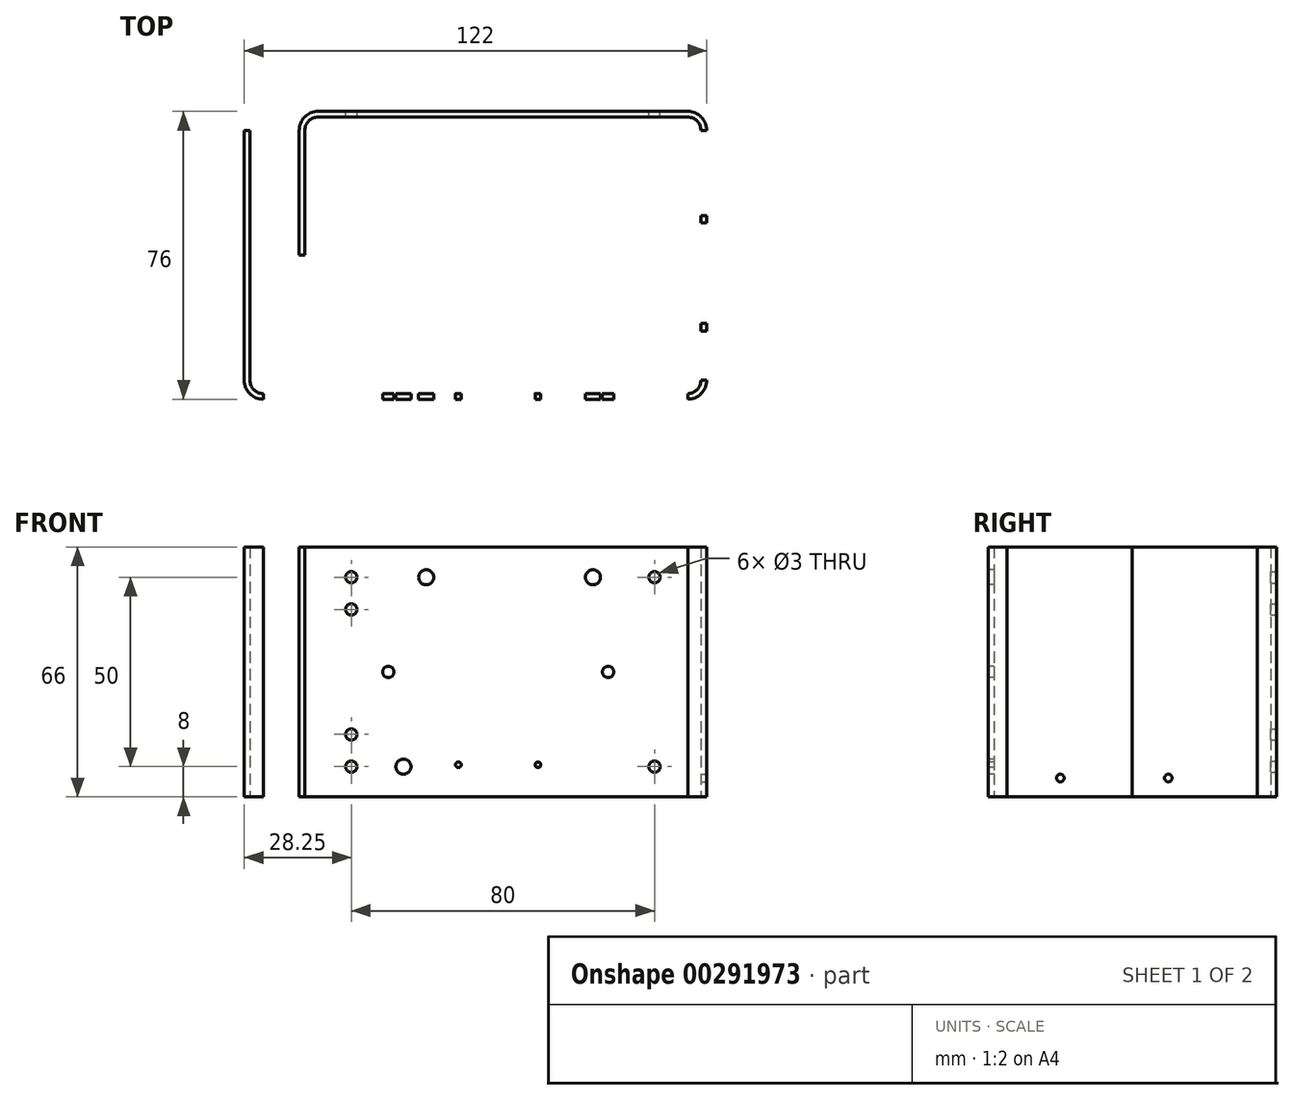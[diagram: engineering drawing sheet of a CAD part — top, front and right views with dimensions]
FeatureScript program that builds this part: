
annotation { "Feature Type Name" : "Feature", "Feature Type Description" : "" }
export const myFeature = defineFeature(function(context is Context, id is Id, definition is map)
    precondition{}
    {
        {
            var Q0;
            Q0=qCreatedBy(makeId("Top.planeOp"),FACE);
            var sketch = newSketch(context, id + "F0", { "sketchPlane" : qUnion([Q0])});
            skLineSegment(sketch, "E0", {"start": v(-66.75, 33) * mm, "end": v(-66.75, -33) * mm});
            skLineSegment(sketch, "E1", {"start": v(-63.25, -36.5) * mm, "end": v(48.75, -36.5) * mm});
            skLineSegment(sketch, "E2", {"start": v(52.25, -33) * mm, "end": v(52.25, 33) * mm});
            skLineSegment(sketch, "E3", {"start": v(48.75, 36.5) * mm, "end": v(-48.75, 36.5) * mm});
            skLineSegment(sketch, "E4", {"start": v(-52.25, 33) * mm, "end": v(-52.25, 0) * mm});
            skLineSegment(sketch, "E5.0", {"start": v(-53.75, 33) * mm, "end": v(-53.75, 0) * mm});
            skLineSegment(sketch, "E5.1", {"start": v(-68.25, 33) * mm, "end": v(-68.25, -33) * mm});
            skLineSegment(sketch, "E5.2", {"start": v(-63.25, -38) * mm, "end": v(48.75, -38) * mm});
            skLineSegment(sketch, "E5.3", {"start": v(53.75, -33) * mm, "end": v(53.75, 33) * mm});
            skLineSegment(sketch, "E5.4", {"start": v(48.75, 38) * mm, "end": v(-48.75, 38) * mm});
            skLineSegment(sketch, "E6", {"start": v(-52.25, 0) * mm, "end": v(-53.75, 0) * mm});
            skLineSegment(sketch, "E7", {"start": v(-66.75, 33) * mm, "end": v(-68.25, 33) * mm});
            skPoint(sketch, "E8.visualSharp", {"position": v(-66.75, -36.5) * mm});
            skArc(sketch, "E8.filletArc", {"start": v(-66.75, -33) * mm, "mid": v(-65.72, -35.47) * mm, "end": v(-63.25, -36.5) * mm});
            skPoint(sketch, "E9.visualSharp", {"position": v(52.25, -36.5) * mm});
            skArc(sketch, "E9.filletArc", {"start": v(48.75, -36.5) * mm, "mid": v(51.22, -35.47) * mm, "end": v(52.25, -33) * mm});
            skPoint(sketch, "E10.visualSharp", {"position": v(52.25, 36.5) * mm});
            skArc(sketch, "E10.filletArc", {"start": v(52.25, 33) * mm, "mid": v(51.22, 35.47) * mm, "end": v(48.75, 36.5) * mm});
            skPoint(sketch, "E11.visualSharp", {"position": v(-52.25, 36.5) * mm});
            skArc(sketch, "E11.filletArc", {"start": v(-48.75, 36.5) * mm, "mid": v(-51.22, 35.47) * mm, "end": v(-52.25, 33) * mm});
            skPoint(sketch, "E12.visualSharp", {"position": v(-68.25, -38) * mm});
            skArc(sketch, "E12.filletArc", {"start": v(-68.25, -33) * mm, "mid": v(-66.79, -36.54) * mm, "end": v(-63.25, -38) * mm});
            skPoint(sketch, "E13.visualSharp", {"position": v(53.75, -38) * mm});
            skArc(sketch, "E13.filletArc", {"start": v(48.75, -38) * mm, "mid": v(52.29, -36.54) * mm, "end": v(53.75, -33) * mm});
            skPoint(sketch, "E14.visualSharp", {"position": v(53.75, 38) * mm});
            skArc(sketch, "E14.filletArc", {"start": v(53.75, 33) * mm, "mid": v(52.29, 36.54) * mm, "end": v(48.75, 38) * mm});
            skPoint(sketch, "E15.visualSharp", {"position": v(-53.75, 38) * mm});
            skArc(sketch, "E15.filletArc", {"start": v(-48.75, 38) * mm, "mid": v(-52.29, 36.54) * mm, "end": v(-53.75, 33) * mm});
            skLineSegment(sketch, "E16", {"start": v(52.25, 0) * mm, "end": v(-12.48, 0) * mm, "construction": true});
            skLineSegment(sketch, "E17", {"start": v(0, 36.5) * mm, "end": v(0, -15.26) * mm, "construction": true});
            skSolve(sketch);
        }
        {
            var Q0;
            Q0=qSketchRegion(id+"F0",true);
            extrude(context, id + "F1", {"entities" : qUnion([Q0]), "depth" : 66 * mm});
        }
        {
            var Q0;
            Q0=makeQuery(id+"F1.opExtrude","SWEPT_FACE",FACE,{"disambiguationData":[OSD([sQuery(id+"F0.wireOp",EDGE,"E5.2")])]});
            var sketch = newSketch(context, id + "F2", { "sketchPlane" : qUnion([Q0])});
            skLineSegment(sketch, "E18.bottom", {"start": v(-23.25, 52) * mm, "end": v(20.75, 52) * mm});
            skLineSegment(sketch, "E18.top", {"start": v(-23.25, 14) * mm, "end": v(20.75, 14) * mm});
            skLineSegment(sketch, "E18.left", {"start": v(-26.25, 49) * mm, "end": v(-26.25, 17) * mm});
            skLineSegment(sketch, "E18.right", {"start": v(23.75, 49) * mm, "end": v(23.75, 17) * mm});
            skLineSegment(sketch, "E19", {"start": v(-63.25, 33) * mm, "end": v(43.75, 33) * mm, "construction": true});
            skLineSegment(sketch, "E20", {"start": v(23.75, 33) * mm, "end": v(-26.25, 33) * mm, "construction": true});
            skLineSegment(sketch, "E21", {"start": v(-1.25, 52) * mm, "end": v(-1.25, 14) * mm, "construction": true});
            skLineSegment(sketch, "E22", {"start": v(-7.25, 66) * mm, "end": v(-7.25, 0) * mm, "construction": true});
            skPoint(sketch, "E23.visualSharp", {"position": v(-26.25, 52) * mm});
            skArc(sketch, "E23.filletArc", {"start": v(-23.25, 52) * mm, "mid": v(-25.37, 51.12) * mm, "end": v(-26.25, 49) * mm});
            skPoint(sketch, "E24.visualSharp", {"position": v(23.75, 52) * mm});
            skArc(sketch, "E24.filletArc", {"start": v(23.75, 49) * mm, "mid": v(22.87, 51.12) * mm, "end": v(20.75, 52) * mm});
            skPoint(sketch, "E25.visualSharp", {"position": v(23.75, 14) * mm});
            skArc(sketch, "E25.filletArc", {"start": v(20.75, 14) * mm, "mid": v(22.87, 14.88) * mm, "end": v(23.75, 17) * mm});
            skPoint(sketch, "E26.visualSharp", {"position": v(-26.25, 14) * mm});
            skArc(sketch, "E26.filletArc", {"start": v(-26.25, 17) * mm, "mid": v(-25.37, 14.88) * mm, "end": v(-23.25, 14) * mm});
            skCircle(sketch, "E27", {"center": v(-30.25, 33) * mm, "radius": 1.5 * mm});
            skCircle(sketch, "E28.MirrorC", {"center": v(27.75, 33) * mm, "radius": 1.5 * mm});
            skCircle(sketch, "E29", {"center": v(-26.25, 58) * mm, "radius": 2 * mm});
            skCircle(sketch, "E30.MirrorC", {"center": v(23.75, 58) * mm, "radius": 2 * mm});
            skCircle(sketch, "E31.MirrorC", {"center": v(-26.25, 8) * mm, "radius": 2 * mm});
            skCircle(sketch, "E32.MirrorC", {"center": v(23.75, 8) * mm, "radius": 2 * mm});
            skLineSegment(sketch, "E33.bottom", {"start": v(-7.25, 7) * mm, "end": v(4.75, 7) * mm});
            skPoint(sketch, "E34.visualSharp", {"position": v(6.25, 10) * mm});
            skLineSegment(sketch, "E33.top", {"start": v(-7.25, 10) * mm, "end": v(4.75, 10) * mm});
            skArc(sketch, "E35.filletArc", {"start": v(-7.25, 10) * mm, "mid": v(-8.31, 9.56) * mm, "end": v(-8.75, 8.5) * mm});
            skLineSegment(sketch, "E33.left", {"start": v(-8.75, 8.5) * mm, "end": v(-8.75, 8.5) * mm});
            skLineSegment(sketch, "E33.right", {"start": v(6.25, 8.5) * mm, "end": v(6.25, 8.5) * mm});
            skArc(sketch, "E36.filletArc", {"start": v(-8.75, 8.5) * mm, "mid": v(-8.31, 7.44) * mm, "end": v(-7.25, 7) * mm});
            skArc(sketch, "E37.filletArc", {"start": v(4.75, 7) * mm, "mid": v(5.81, 7.44) * mm, "end": v(6.25, 8.5) * mm});
            skArc(sketch, "E34.filletArc", {"start": v(6.25, 8.5) * mm, "mid": v(5.81, 9.56) * mm, "end": v(4.75, 10) * mm});
            skCircle(sketch, "E38", {"center": v(-11.75, 8.5) * mm, "radius": 0.75 * mm});
            skPoint(sketch, "E39", {"position": v(-1.25, 10) * mm});
            skLineSegment(sketch, "E40", {"start": v(-11.75, 8.5) * mm, "end": v(6.89, 8.5) * mm, "construction": true});
            skPoint(sketch, "E35.visualSharp", {"position": v(-8.75, 10) * mm});
            skPoint(sketch, "E36.visualSharp", {"position": v(-8.75, 7) * mm});
            skPoint(sketch, "E37.visualSharp", {"position": v(6.25, 7) * mm});
            skLineSegment(sketch, "E41", {"start": v(-1.25, 10) * mm, "end": v(-1.25, 7) * mm, "construction": true});
            skCircle(sketch, "E42.MirrorC", {"center": v(9.25, 8.5) * mm, "radius": 0.75 * mm});
            skLineSegment(sketch, "E43", {"start": v(-26.25, 8) * mm, "end": v(-26.25, 58) * mm, "construction": true});
            skLineSegment(sketch, "E44", {"start": v(23.75, 58) * mm, "end": v(23.75, 8) * mm, "construction": true});
            skLineSegment(sketch, "E45", {"start": v(-26.25, 8) * mm, "end": v(23.75, 8) * mm, "construction": true});
            skLineSegment(sketch, "E46", {"start": v(23.75, 58) * mm, "end": v(-26.25, 58) * mm, "construction": true});
            skCircle(sketch, "E47", {"center": v(-20.25, 8) * mm, "radius": 2 * mm});
            skCircle(sketch, "E48.MirrorC", {"center": v(-20.25, 58) * mm, "radius": 2 * mm});
            skCircle(sketch, "E49.MirrorC", {"center": v(17.75, 58) * mm, "radius": 2 * mm});
            skCircle(sketch, "E50", {"center": v(14.75, 8) * mm, "radius": 2 * mm});
            skPoint(sketch, "E51", {"position": v(-63.25, 33) * mm});
            skSolve(sketch);
        }
        {
            var Q0;
            Q0=makeQuery(id+"F2.imprint","IMPRINT",FACE,{"disambiguationData":[TD([[makeQuery(id+"F2.imprint","IMPRINT",EDGE,{"derivedFrom":sQuery(id+"F2.wireOp",EDGE,"E18.bottom")}),-1.0]])]});
            var Q1;
            Q1=makeQuery(id+"F2.imprint","IMPRINT",FACE,{"disambiguationData":[TD([[makeQuery(id+"F2.imprint","IMPRINT",EDGE,{"derivedFrom":sQuery(id+"F2.wireOp",EDGE,"5223969e-9384-4705-a09f-08a9d0864926")}),1.0]])]});
            var Q2;
            Q2=makeQuery(id+"F2.imprint","IMPRINT",FACE,{"disambiguationData":[TD([[makeQuery(id+"F2.imprint","IMPRINT",EDGE,{"derivedFrom":sQuery(id+"F2.wireOp",EDGE,"b6238159-0034-45e9-8c88-9dabcd8353630.MirrorC")}),-1.0]])]});
            var Q3;
            Q3=makeQuery(id+"F2.imprint","IMPRINT",FACE,{"disambiguationData":[TD([[makeQuery(id+"F2.imprint","IMPRINT",EDGE,{"derivedFrom":sQuery(id+"F2.wireOp",EDGE,"E29")}),1.0]])]});
            var Q4;
            Q4=makeQuery(id+"F2.imprint","IMPRINT",FACE,{"disambiguationData":[TD([[makeQuery(id+"F2.imprint","IMPRINT",EDGE,{"derivedFrom":sQuery(id+"F2.wireOp",EDGE,"E30.MirrorC")}),-1.0]])]});
            var Q5;
            Q5=makeQuery(id+"F2.imprint","IMPRINT",FACE,{"disambiguationData":[TD([[makeQuery(id+"F2.imprint","IMPRINT",EDGE,{"derivedFrom":sQuery(id+"F2.wireOp",EDGE,"E32.MirrorC")}),1.0]])]});
            var Q6;
            Q6=makeQuery(id+"F2.imprint","IMPRINT",FACE,{"disambiguationData":[TD([[makeQuery(id+"F2.imprint","IMPRINT",EDGE,{"derivedFrom":sQuery(id+"F2.wireOp",EDGE,"E31.MirrorC")}),-1.0]])]});
            var Q7;
            Q7=makeQuery(id+"F2.imprint","IMPRINT",FACE,{"disambiguationData":[TD([[makeQuery(id+"F2.imprint","IMPRINT",EDGE,{"derivedFrom":sQuery(id+"F2.wireOp",EDGE,"E33.bottom")}),1.0]])]});
            var Q8;
            Q8=makeQuery(id+"F2.imprint","IMPRINT",FACE,{"disambiguationData":[TD([[makeQuery(id+"F2.imprint","IMPRINT",EDGE,{"derivedFrom":sQuery(id+"F2.wireOp",EDGE,"E47")}),1.0]])]});
            var Q9;
            Q9=makeQuery(id+"F2.imprint","IMPRINT",FACE,{"disambiguationData":[TD([[makeQuery(id+"F2.imprint","IMPRINT",EDGE,{"derivedFrom":sQuery(id+"F2.wireOp",EDGE,"E48.MirrorC")}),-1.0]])]});
            var Q10;
            Q10=makeQuery(id+"F2.imprint","IMPRINT",FACE,{"disambiguationData":[TD([[makeQuery(id+"F2.imprint","IMPRINT",EDGE,{"derivedFrom":sQuery(id+"F2.wireOp",EDGE,"E49.MirrorC")}),1.0]])]});
            var Q11;
            Q11=makeQuery(id+"F2.imprint","IMPRINT",FACE,{"disambiguationData":[TD([[makeQuery(id+"F2.imprint","IMPRINT",EDGE,{"derivedFrom":sQuery(id+"F2.wireOp",EDGE,"E50")}),1.0]])]});
            extrude(context, id + "F3", {"entities" : qUnion([Q0, Q1, Q2, Q3, Q4, Q5, Q6, Q7, Q8, Q9, Q10, Q11]), "operationType" : NewBodyOperationType.REMOVE, "oppositeDirection" : true, "depth" : 25 * mm});
        }
        {
            var Q0;
            Q0=makeQuery(id+"F1.opExtrude","SWEPT_FACE",FACE,{"disambiguationData":[OSD([sQuery(id+"F0.wireOp",EDGE,"E5.4")])]});
            var sketch = newSketch(context, id + "F4", { "sketchPlane" : qUnion([Q0])});
            skCircle(sketch, "E52", {"center": v(-40, 58) * mm, "radius": 1.5 * mm});
            skLineSegment(sketch, "E53", {"start": v(-40, 58) * mm, "end": v(-40, 8) * mm, "construction": true});
            skLineSegment(sketch, "E54", {"start": v(-40, 8) * mm, "end": v(40, 8) * mm, "construction": true});
            skLineSegment(sketch, "E55", {"start": v(40, 8) * mm, "end": v(40, 58) * mm, "construction": true});
            skLineSegment(sketch, "E56", {"start": v(40, 58) * mm, "end": v(-40, 58) * mm, "construction": true});
            skCircle(sketch, "E57", {"center": v(-40, 8) * mm, "radius": 1.5 * mm});
            skCircle(sketch, "E58", {"center": v(40, 8) * mm, "radius": 1.5 * mm});
            skCircle(sketch, "E59", {"center": v(40, 58) * mm, "radius": 1.5 * mm});
            skLineSegment(sketch, "E60", {"start": v(0, 0) * mm, "end": v(0, 116) * mm, "construction": true});
            skPoint(sketch, "E60.endSnap0", {"position": v(0, 0) * mm});
            skPoint(sketch, "E61", {"position": v(0, 58) * mm});
            skCircle(sketch, "E62", {"center": v(40, 49.5) * mm, "radius": 1.5 * mm});
            skCircle(sketch, "E63", {"center": v(40, 16.5) * mm, "radius": 1.5 * mm});
            skLineSegment(sketch, "E64", {"start": v(33.75, 66) * mm, "end": v(33.75, 0) * mm, "construction": true});
            skLineSegment(sketch, "E65", {"start": v(33.75, 33) * mm, "end": v(24.95, 33) * mm, "construction": true});
            skLineSegment(sketch, "E66", {"start": v(29.35, 33) * mm, "end": v(29.35, 66) * mm, "construction": true});
            skLineSegment(sketch, "E67", {"start": v(29.35, 33) * mm, "end": v(29.35, 0) * mm, "construction": true});
            skLineSegment(sketch, "E68", {"start": v(29.35, 16.5) * mm, "end": v(44.25, 16.5) * mm, "construction": true});
            skLineSegment(sketch, "E69", {"start": v(29.35, 49.5) * mm, "end": v(45.75, 49.5) * mm, "construction": true});
            skSolve(sketch);
        }
        {
            var Q0;
            Q0=makeQuery(id+"F4.imprint","IMPRINT",FACE,{"disambiguationData":[TD([[makeQuery(id+"F4.imprint","IMPRINT",EDGE,{"derivedFrom":sQuery(id+"F4.wireOp",EDGE,"E52")}),1.0]])]});
            var Q1;
            Q1=makeQuery(id+"F4.imprint","IMPRINT",FACE,{"disambiguationData":[TD([[makeQuery(id+"F4.imprint","IMPRINT",EDGE,{"derivedFrom":sQuery(id+"F4.wireOp",EDGE,"E57")}),1.0]])]});
            var Q2;
            Q2=makeQuery(id+"F4.imprint","IMPRINT",FACE,{"disambiguationData":[TD([[makeQuery(id+"F4.imprint","IMPRINT",EDGE,{"derivedFrom":sQuery(id+"F4.wireOp",EDGE,"E58")}),1.0]])]});
            var Q3;
            Q3=makeQuery(id+"F4.imprint","IMPRINT",FACE,{"disambiguationData":[TD([[makeQuery(id+"F4.imprint","IMPRINT",EDGE,{"derivedFrom":sQuery(id+"F4.wireOp",EDGE,"E59")}),1.0]])]});
            var Q4;
            Q4=makeQuery(id+"F4.imprint","IMPRINT",FACE,{"disambiguationData":[TD([[makeQuery(id+"F4.imprint","IMPRINT",EDGE,{"derivedFrom":sQuery(id+"F4.wireOp",EDGE,"E63")}),1.0]])]});
            var Q5;
            Q5=makeQuery(id+"F4.imprint","IMPRINT",FACE,{"disambiguationData":[TD([[makeQuery(id+"F4.imprint","IMPRINT",EDGE,{"derivedFrom":sQuery(id+"F4.wireOp",EDGE,"E62")}),1.0]])]});
            extrude(context, id + "F5", {"entities" : qUnion([Q0, Q1, Q2, Q3, Q4, Q5]), "operationType" : NewBodyOperationType.REMOVE, "oppositeDirection" : true, "depth" : 25 * mm});
        }
        {
            var Q0;
            Q0=makeQuery(id+"F1.opExtrude","SWEPT_FACE",FACE,{"disambiguationData":[OSD([sQuery(id+"F0.wireOp",EDGE,"E5.3")])]});
            var sketch = newSketch(context, id + "F6", { "sketchPlane" : qUnion([Q0])});
            skLineSegment(sketch, "E70.bottom", {"start": v(-21, 58) * mm, "end": v(-17, 58) * mm});
            skLineSegment(sketch, "E70.top", {"start": v(-21, 8) * mm, "end": v(-17, 8) * mm});
            skLineSegment(sketch, "E70.left", {"start": v(-24, 55) * mm, "end": v(-24, 11) * mm});
            skLineSegment(sketch, "E70.right", {"start": v(-14, 55) * mm, "end": v(-14, 11) * mm});
            skLineSegment(sketch, "E71.bottom", {"start": v(-5, 58) * mm, "end": v(24, 58) * mm});
            skLineSegment(sketch, "E71.top", {"start": v(-5, 8) * mm, "end": v(24, 8) * mm});
            skLineSegment(sketch, "E71.left", {"start": v(-8, 55) * mm, "end": v(-8, 11) * mm});
            skLineSegment(sketch, "E71.right", {"start": v(27, 55) * mm, "end": v(27, 11) * mm});
            skLineSegment(sketch, "E72", {"start": v(-14, 58) * mm, "end": v(-8, 58) * mm, "construction": true});
            skLineSegment(sketch, "E73", {"start": v(-14, 8) * mm, "end": v(-8, 8) * mm, "construction": true});
            skPoint(sketch, "E74.visualSharp", {"position": v(-24, 58) * mm});
            skArc(sketch, "E74.filletArc", {"start": v(-21, 58) * mm, "mid": v(-23.12, 57.12) * mm, "end": v(-24, 55) * mm});
            skPoint(sketch, "E75.visualSharp", {"position": v(-14, 58) * mm});
            skArc(sketch, "E75.filletArc", {"start": v(-14, 55) * mm, "mid": v(-14.88, 57.12) * mm, "end": v(-17, 58) * mm});
            skPoint(sketch, "E76.visualSharp", {"position": v(-24, 8) * mm});
            skArc(sketch, "E76.filletArc", {"start": v(-24, 11) * mm, "mid": v(-23.12, 8.88) * mm, "end": v(-21, 8) * mm});
            skPoint(sketch, "E77.visualSharp", {"position": v(-14, 8) * mm});
            skArc(sketch, "E77.filletArc", {"start": v(-17, 8) * mm, "mid": v(-14.88, 8.88) * mm, "end": v(-14, 11) * mm});
            skPoint(sketch, "E78.visualSharp", {"position": v(-8, 8) * mm});
            skArc(sketch, "E78.filletArc", {"start": v(-8, 11) * mm, "mid": v(-7.12, 8.88) * mm, "end": v(-5, 8) * mm});
            skPoint(sketch, "E79.visualSharp", {"position": v(27, 8) * mm});
            skArc(sketch, "E79.filletArc", {"start": v(24, 8) * mm, "mid": v(26.12, 8.88) * mm, "end": v(27, 11) * mm});
            skPoint(sketch, "E80.visualSharp", {"position": v(27, 58) * mm});
            skArc(sketch, "E80.filletArc", {"start": v(27, 55) * mm, "mid": v(26.12, 57.12) * mm, "end": v(24, 58) * mm});
            skPoint(sketch, "E81.visualSharp", {"position": v(-8, 58) * mm});
            skArc(sketch, "E81.filletArc", {"start": v(-5, 58) * mm, "mid": v(-7.12, 57.12) * mm, "end": v(-8, 55) * mm});
            skCircle(sketch, "E82", {"center": v(-19, 61) * mm, "radius": 1 * mm});
            skLineSegment(sketch, "E83", {"start": v(-24, 33) * mm, "end": v(27, 33) * mm, "construction": true});
            skLineSegment(sketch, "E84", {"start": v(-19, 58) * mm, "end": v(-19, 8) * mm, "construction": true});
            skPoint(sketch, "E84.endSnap0", {"position": v(-19, 8) * mm});
            skLineSegment(sketch, "E85", {"start": v(9.5, 8) * mm, "end": v(9.5, 58) * mm, "construction": true});
            skCircle(sketch, "E86", {"center": v(9.5, 61) * mm, "radius": 1 * mm});
            skCircle(sketch, "E87.MirrorC", {"center": v(-19, 5) * mm, "radius": 1 * mm});
            skCircle(sketch, "E88.MirrorC", {"center": v(9.5, 5) * mm, "radius": 1 * mm});
            skSolve(sketch);
        }
        {
            var Q0;
            Q0=makeQuery(id+"F6.imprint","IMPRINT",FACE,{"disambiguationData":[TD([[makeQuery(id+"F6.imprint","IMPRINT",EDGE,{"derivedFrom":sQuery(id+"F6.wireOp",EDGE,"E70.bottom")}),-1.0]])]});
            var Q1;
            Q1=makeQuery(id+"F6.imprint","IMPRINT",FACE,{"disambiguationData":[TD([[makeQuery(id+"F6.imprint","IMPRINT",EDGE,{"derivedFrom":sQuery(id+"F6.wireOp",EDGE,"E71.bottom")}),-1.0]])]});
            var Q2;
            Q2=makeQuery(id+"F6.imprint","IMPRINT",FACE,{"disambiguationData":[TD([[makeQuery(id+"F6.imprint","IMPRINT",EDGE,{"derivedFrom":sQuery(id+"F6.wireOp",EDGE,"E70.bottom")}),-1.0]])]});
            var Q3;
            Q3=makeQuery(id+"F6.imprint","IMPRINT",FACE,{"disambiguationData":[TD([[makeQuery(id+"F6.imprint","IMPRINT",EDGE,{"derivedFrom":sQuery(id+"F6.wireOp",EDGE,"E71.bottom")}),-1.0]])]});
            var Q4;
            Q4=makeQuery(id+"F6.imprint","IMPRINT",FACE,{"disambiguationData":[TD([[makeQuery(id+"F6.imprint","IMPRINT",EDGE,{"derivedFrom":sQuery(id+"F6.wireOp",EDGE,"E82")}),1.0]])]});
            var Q5;
            Q5=makeQuery(id+"F6.imprint","IMPRINT",FACE,{"disambiguationData":[TD([[makeQuery(id+"F6.imprint","IMPRINT",EDGE,{"derivedFrom":sQuery(id+"F6.wireOp",EDGE,"E86")}),1.0]])]});
            var Q6;
            Q6=makeQuery(id+"F6.imprint","IMPRINT",FACE,{"disambiguationData":[TD([[makeQuery(id+"F6.imprint","IMPRINT",EDGE,{"derivedFrom":sQuery(id+"F6.wireOp",EDGE,"E88.MirrorC")}),-1.0]])]});
            var Q7;
            Q7=makeQuery(id+"F6.imprint","IMPRINT",FACE,{"disambiguationData":[TD([[makeQuery(id+"F6.imprint","IMPRINT",EDGE,{"derivedFrom":sQuery(id+"F6.wireOp",EDGE,"E87.MirrorC")}),-1.0]])]});
            extrude(context, id + "F7", {"entities" : qUnion([Q0, Q1, Q2, Q3, Q4, Q5, Q6, Q7]), "operationType" : NewBodyOperationType.REMOVE, "oppositeDirection" : true, "depth" : 25 * mm});
        }
    });
